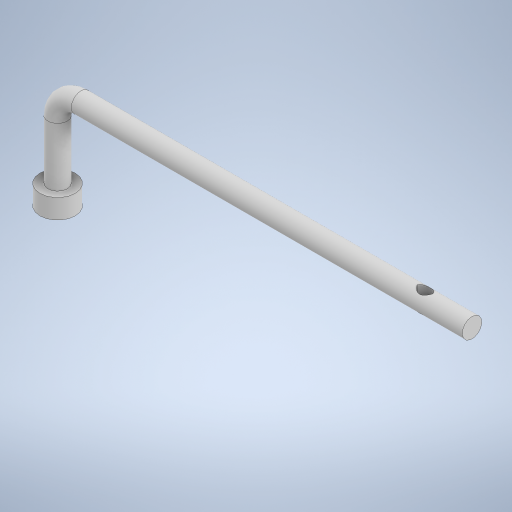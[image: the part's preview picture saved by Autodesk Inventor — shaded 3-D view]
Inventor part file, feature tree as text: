
AUTODESK INVENTOR PART (.ipt)
format: ipt  version: 2024 (Build 280153000, 153)  size: 293,888 bytes
history: native  units: mm
features: sketch x5, extrude x3, revolve x2
ambient origin geometry x8: Origin, YZ Plane, XZ Plane, XY Plane, X Axis, Y Axis, Z Axis, Center Point
bodies: Solid1 (feature_tree)
feature tree (10):
  sketch  "Sketch1"  dims[d8=25.0mm d9=500.0mm d10=0.0mm]
  extrude  "Extrusion1"  Depth=500.0mm TaperAngle=0.0deg
  extrude  "Extrusion2"  TaperAngle=90.0deg  [1 undecoded]
  revolve  "Revolution1"  [1 undecoded]
  revolve  "Revolution2"  [1 undecoded]
  extrude  "Extrusion3"  TaperAngle=90.0deg  [1 undecoded]
  sketch  "Sketch2"  dims[d11=25.0mm d12=0.0mm d13=90.0deg]
  sketch  "Sketch3"  dims[d14=30.0mm d15=75.0mm]
  sketch  "Sketch5"  dims[d16=10.0mm d17=25.0mm]
  sketch  "Sketch6"  dims[d18=22.5mm d19=90.0deg d23=90.0deg d24=120.0deg d25=21.0mm d26=120.0deg d27=120.0deg d28=0.0mm d29=120.0deg d30=0.0mm d31=10.5mm d32=10.5mm d33=20.0mm d34=0.0mm]
note: 4 required parameter values undecoded (feature->parameter linkage not recoverable at this tier; creation-order binding heuristic only, values carry confidence <= 0.55)